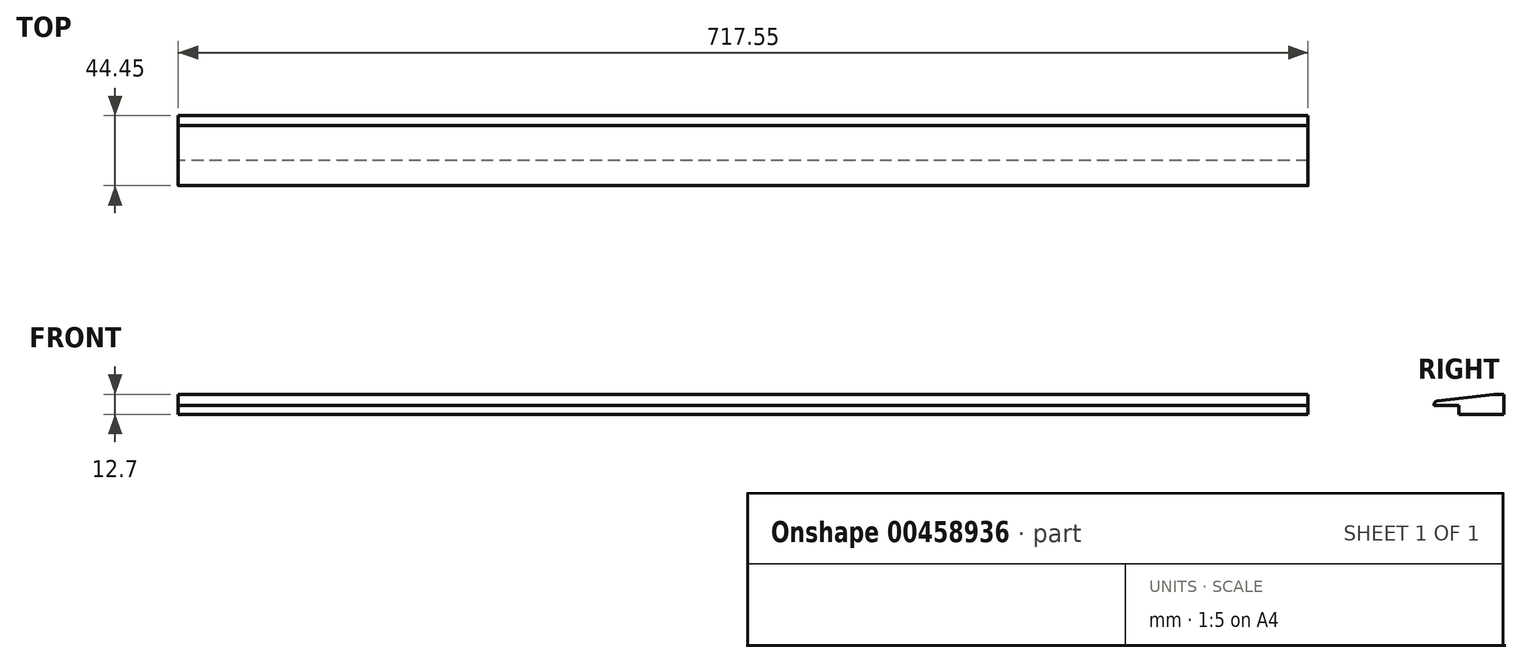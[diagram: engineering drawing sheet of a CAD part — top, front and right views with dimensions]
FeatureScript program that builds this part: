
annotation { "Feature Type Name" : "Feature", "Feature Type Description" : "" }
export const myFeature = defineFeature(function(context is Context, id is Id, definition is map)
    precondition{}
    {
        {
            var Q0;
            Q0=qCreatedBy(makeId("Right.planeOp"),FACE);
            var sketch = newSketch(context, id + "F0", { "sketchPlane" : qUnion([Q0])});
            skLineSegment(sketch, "E0.bottom", {"start": v(15.88, -0.07) * mm, "end": v(44.45, -0.07) * mm});
            skLineSegment(sketch, "E0.top", {"start": v(38.1, 12.63) * mm, "end": v(44.45, 12.63) * mm});
            skLineSegment(sketch, "E0.left", {"start": v(0, 5.51) * mm, "end": v(0, 5.8) * mm});
            skLineSegment(sketch, "E0.right", {"start": v(44.45, -0.07) * mm, "end": v(44.45, 12.63) * mm});
            skLineSegment(sketch, "E1.top", {"start": v(0, 5.51) * mm, "end": v(15.88, 5.51) * mm});
            skLineSegment(sketch, "E1.right", {"start": v(15.88, -0.07) * mm, "end": v(15.88, 5.51) * mm});
            skLineSegment(sketch, "E2", {"start": v(2.24, 8.32) * mm, "end": v(38.1, 12.63) * mm});
            skPoint(sketch, "E3.visualSharp", {"position": v(0, 8.05) * mm});
            skArc(sketch, "E3.filletArc", {"start": v(2.24, 8.32) * mm, "mid": v(0.64, 7.49) * mm, "end": v(0, 5.8) * mm});
            skSolve(sketch);
        }
        {
            var Q0;
            Q0 = qSketchRegion(id + "F0", true);
            extrude(context, id + "F1", {"entities" : qUnion([Q0]), "depth" : 717.55 * mm});
        }
    });
